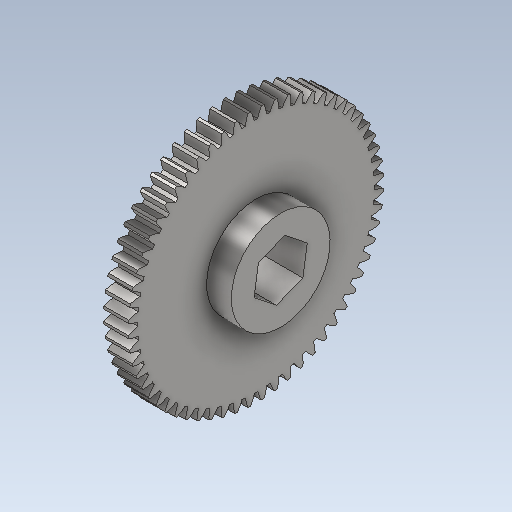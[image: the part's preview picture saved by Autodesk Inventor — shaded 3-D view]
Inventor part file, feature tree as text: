
AUTODESK INVENTOR PART (.ipt)
format: ipt  version: 2023 (Build 270158000, 158)  size: 501,760 bytes
history: native  units: in
note: dims shown in document units (in); Inventor stores cm internally (conversion verified against a paired STEP export)
features: other x3, sketch x3
ambient origin geometry x8: Origin, YZ Plane, XZ Plane, XY Plane, X Axis, Y Axis, Z Axis, Center Point
bodies: Solid1 (feature_tree)
feature tree (6):
  other  "CH-1-01-60T_Idler.ipt"
  other  "Solid1::CH-1-01-60T_Idler.ipt"
  other  "TaggingFeature1"
  sketch  "Sketch3"  dims[d0=0.3937in]
  sketch  "Sketch5"
  sketch  "Sketch4"
